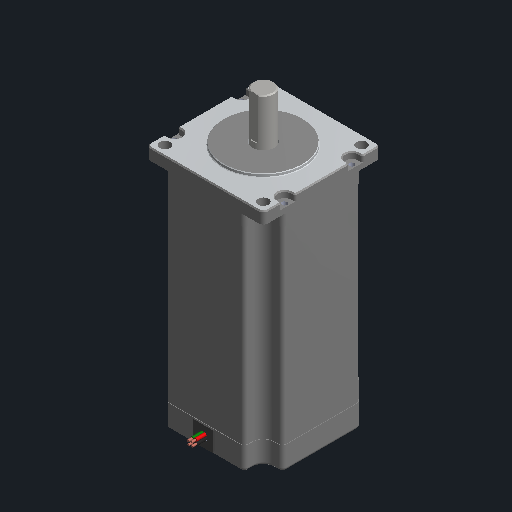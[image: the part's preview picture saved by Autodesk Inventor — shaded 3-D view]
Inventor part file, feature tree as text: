
AUTODESK INVENTOR PART (.ipt)
format: ipt  version: 2022 (Build 260153000, 153)  size: 342,528 bytes
history: native  units: mm (DEFAULTED — no unit token found)
features: other x10, extrude x2, sketch x2, chamfer x1, projected_geometry x1
ambient origin geometry x8: Origin, YZ Plane, XZ Plane, XY Plane, X Axis, Y Axis, Z Axis, Center Point
bodies: Solid1 (feature_tree), Solid2 (feature_tree), Solid3 (feature_tree), Solid4 (feature_tree), Solid5 (feature_tree), Solid6 (feature_tree), Solid7 (feature_tree), Solid8 (feature_tree), Solid9 (feature_tree), Solid10 (feature_tree)
feature tree (16):
  extrude  "Extrusion1"  Depth=2.0mm TaperAngle=0.0deg
  chamfer  "Chamfer1"  Distance=22.0mm
  extrude  "Extrusion2"  Depth=2.0mm
  sketch  "Sketch1"  dims[d0=10.0mm d1=2.0mm d2=0.0mm d3=22.0mm d4=0.0mm]
  sketch  "Sketch2"  dims[d5=0.5mm d6=2.0mm d7=45.0deg d8=9.5mm d9=20.0mm d10=0.0mm]
  projected_geometry  "Projected Loop1"
  other  "Boss-Extrude7"
  other  "Boss-Extrude8[1]"
  other  "Boss-Extrude8[2]"
  other  "Boss-Extrude8[3]"
  other  "Boss-Extrude8[4]"
  other  "Boss-Extrude9[1]"
  other  "Boss-Extrude9[2]"
  other  "Boss-Extrude9[3]"
  other  "Boss-Extrude9[4]"
  other  "M3 Tapped Hole2"
